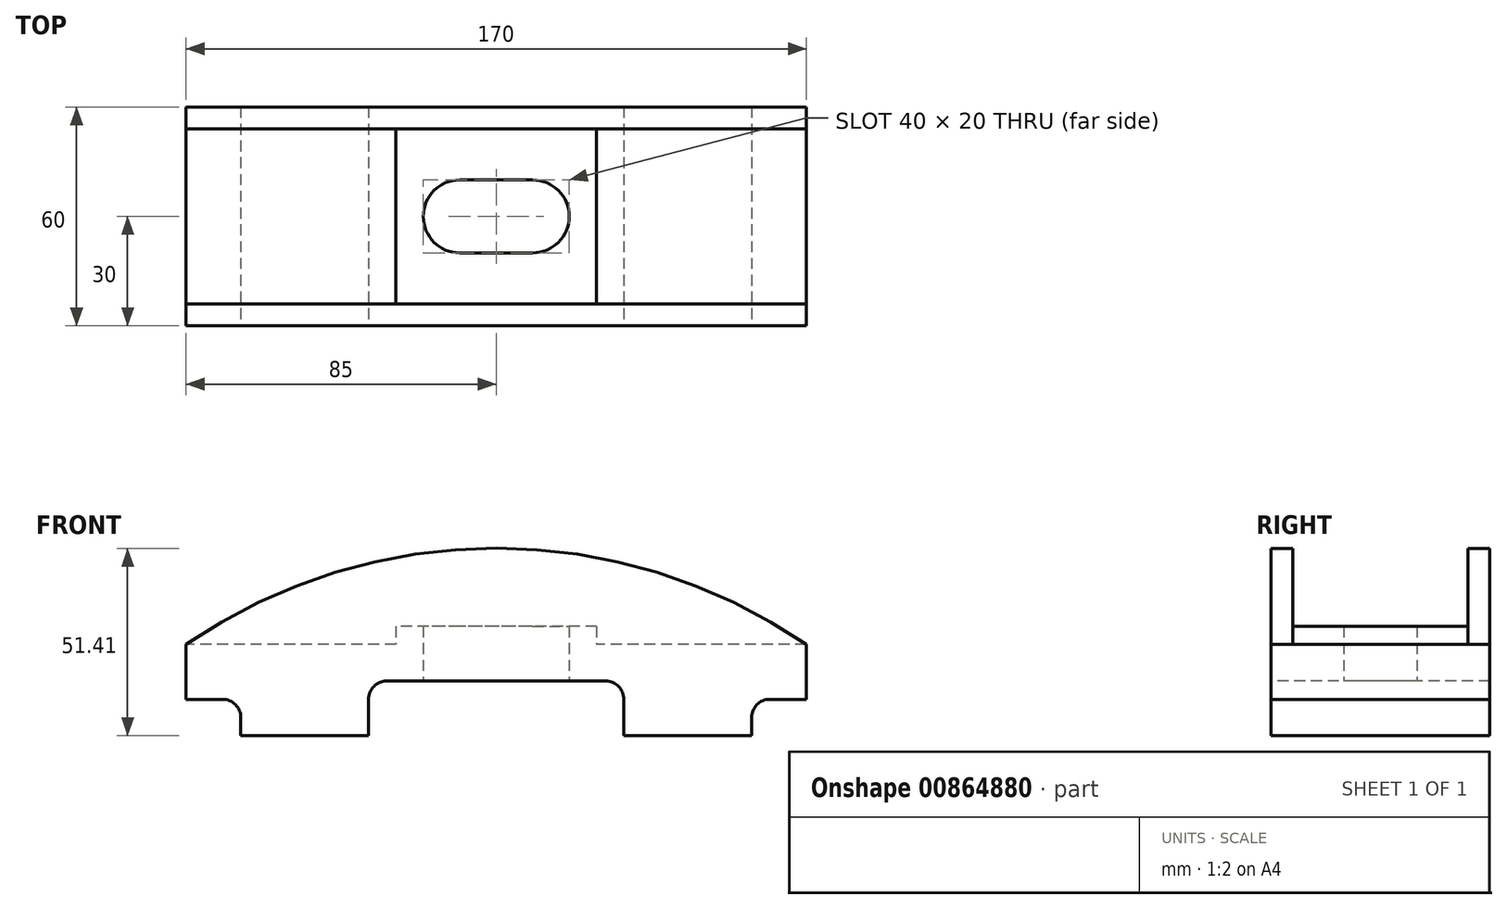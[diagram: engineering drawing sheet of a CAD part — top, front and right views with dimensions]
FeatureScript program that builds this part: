
annotation { "Feature Type Name" : "Feature", "Feature Type Description" : "" }
export const myFeature = defineFeature(function(context is Context, id is Id, definition is map)
    precondition{}
    {
        {
            var Q0;
            Q0=qCreatedBy(makeId("Top.planeOp"),FACE);
            var sketch = newSketch(context, id + "F0", { "sketchPlane" : qUnion([Q0])});
            skLineSegment(sketch, "E0.bottom", {"start": v(85, -30) * mm, "end": v(-85, -30) * mm});
            skLineSegment(sketch, "E0.top", {"start": v(85, 30) * mm, "end": v(-85, 30) * mm});
            skLineSegment(sketch, "E0.left", {"start": v(85, -30) * mm, "end": v(85, 30) * mm});
            skLineSegment(sketch, "E0.right", {"start": v(-85, -30) * mm, "end": v(-85, 30) * mm});
            skPoint(sketch, "E0.middle", {"position": v(0, 0) * mm});
            skSolve(sketch);
        }
        {
            var Q0;
            Q0 = qSketchRegion(id + "F0", true);
            extrude(context, id + "F1", {"entities" : qUnion([Q0]), "oppositeDirection" : true, "depth" : 25 * mm, "offsetDistance" : 25 * mm});
        }
        {
            var Q0;
            Q0=makeQuery(id+"F1.opExtrude","CAP_FACE",FACE,{"disambiguationData":[OSD([sQuery(id+"F0.wireOp",EDGE,"E0.bottom"),sQuery(id+"F0.wireOp",EDGE,"E0.top"),sQuery(id+"F0.wireOp",EDGE,"E0.left"),sQuery(id+"F0.wireOp",EDGE,"E0.right")])],"isStart":true});
            var sketch = newSketch(context, id + "F2", { "sketchPlane" : qUnion([Q0])});
            skLineSegment(sketch, "E1.bottom", {"start": v(27.5, -24) * mm, "end": v(-27.5, -24) * mm});
            skLineSegment(sketch, "E1.top", {"start": v(27.5, 24) * mm, "end": v(-27.5, 24) * mm});
            skLineSegment(sketch, "E1.left", {"start": v(27.5, -24) * mm, "end": v(27.5, 24) * mm});
            skLineSegment(sketch, "E1.right", {"start": v(-27.5, -24) * mm, "end": v(-27.5, 24) * mm});
            skPoint(sketch, "E1.middle", {"position": v(0, 0) * mm});
            skLineSegment(sketch, "E2.bottom", {"start": v(10, -10) * mm, "end": v(-10, -10) * mm});
            skLineSegment(sketch, "E2.top", {"start": v(10, 10) * mm, "end": v(-10, 10) * mm});
            skLineSegment(sketch, "E2.left", {"start": v(10, -10) * mm, "end": v(10, 10) * mm});
            skLineSegment(sketch, "E2.right", {"start": v(-10, -10) * mm, "end": v(-10, 10) * mm});
            skCircle(sketch, "E3", {"center": v(-10, 0) * mm, "radius": 10 * mm});
            skCircle(sketch, "E4", {"center": v(10, 0) * mm, "radius": 10 * mm});
            skSolve(sketch);
        }
        {
            var Q0;
            Q0=makeQuery(id+"F2.imprint","IMPRINT",FACE,{"disambiguationData":[TD([[makeQuery(id+"F2.imprint","IMPRINT",EDGE,{"derivedFrom":sQuery(id+"F2.wireOp",EDGE,"E1.bottom")}),-1.0]])]});
            extrude(context, id + "F3", {"entities" : qUnion([Q0]), "operationType" : NewBodyOperationType.ADD, "depth" : 5 * mm, "offsetDistance" : 25 * mm});
        }
        {
            var Q0;
            Q0=makeQuery(id+"F3.boolean.opBoolean","SPLIT",FACE,{"disambiguationData":[TD([makeQuery(id+"F3.opExtrude","SWEPT_FACE",FACE,{"disambiguationData":[OSD([sQuery(id+"F2.wireOp",EDGE,"E2.bottom")])]})])],"derivedFrom":makeQuery(id+"F1.opExtrude","CAP_FACE",FACE,{"disambiguationData":[OSD([sQuery(id+"F0.wireOp",EDGE,"E0.bottom"),sQuery(id+"F0.wireOp",EDGE,"E0.top"),sQuery(id+"F0.wireOp",EDGE,"E0.left"),sQuery(id+"F0.wireOp",EDGE,"E0.right")])],"isStart":true})});
            extrude(context, id + "F4", {"entities" : qUnion([Q0]), "operationType" : NewBodyOperationType.REMOVE, "endBound" : BoundingType.THROUGH_ALL, "oppositeDirection" : true, "depth" : 25 * mm, "offsetDistance" : 25 * mm});
        }
        {
            var Q0;
            Q0=makeQuery(id+"F1.opExtrude","SWEPT_FACE",FACE,{"disambiguationData":[OSD([sQuery(id+"F0.wireOp",EDGE,"E0.bottom")])]});
            var sketch = newSketch(context, id + "F5", { "sketchPlane" : qUnion([Q0])});
            skArc(sketch, "E5", {"start": v(85, 0) * mm, "mid": v(0, 26.4) * mm, "end": v(-85, 0) * mm});
            skSolve(sketch);
        }
        {
            var Q0;
            Q0=makeQuery(id+"F1.opExtrude","SWEPT_FACE",FACE,{"disambiguationData":[OSD([sQuery(id+"F0.wireOp",EDGE,"E0.top")])]});
            var sketch = newSketch(context, id + "F6", { "sketchPlane" : qUnion([Q0])});
            skArc(sketch, "E6", {"start": v(85, 0) * mm, "mid": v(0, 26.4) * mm, "end": v(-85, 0) * mm});
            skSolve(sketch);
        }
        {
            var Q0;
            Q0=makeQuery(id+"F6.imprint","IMPRINT",FACE,{"disambiguationData":[TD([[makeQuery(id+"F6.imprint","IMPRINT",EDGE,{"derivedFrom":sQuery(id+"F6.wireOp",EDGE,"E6")}),1.0]])]});
            extrude(context, id + "F7", {"entities" : qUnion([Q0]), "operationType" : NewBodyOperationType.ADD, "oppositeDirection" : true, "depth" : 6 * mm, "offsetDistance" : 25 * mm});
        }
        {
            var Q0;
            Q0=makeQuery(id+"F5.imprint","IMPRINT",FACE,{"disambiguationData":[TD([[makeQuery(id+"F5.imprint","IMPRINT",EDGE,{"derivedFrom":sQuery(id+"F5.wireOp",EDGE,"E5")}),1.0]])]});
            extrude(context, id + "F8", {"entities" : qUnion([Q0]), "operationType" : NewBodyOperationType.ADD, "oppositeDirection" : true, "depth" : 6 * mm, "offsetDistance" : 25 * mm});
        }
        {
            var Q0;
            {var subQ0=sQuery(id+"F0.wireOp",EDGE,"E0.bottom");Q0=makeQuery(id+"F8.boolean.opBoolean","MERGE",FACE,{"derivedFrom":[makeQuery(id+"F1.opExtrude","SWEPT_FACE",FACE,{"disambiguationData":[OSD([subQ0])]}),makeQuery(id+"F8.opExtrude","CAP_FACE",FACE,{"disambiguationData":[OSD([subQ0,sQuery(id+"F5.wireOp",EDGE,"E5")])],"isStart":true})]});}
            var sketch = newSketch(context, id + "F9", { "sketchPlane" : qUnion([Q0])});
            skLineSegment(sketch, "E7", {"start": v(0, -25) * mm, "end": v(-35, -25) * mm});
            skLineSegment(sketch, "E8", {"start": v(0, -25) * mm, "end": v(35, -25) * mm});
            skLineSegment(sketch, "E9", {"start": v(-35, -25) * mm, "end": v(-35, -15) * mm});
            skLineSegment(sketch, "E10", {"start": v(-30, -10) * mm, "end": v(30, -10) * mm});
            skLineSegment(sketch, "E11", {"start": v(35, -15) * mm, "end": v(35, -25) * mm});
            skPoint(sketch, "E12.visualSharp", {"position": v(-35, -10) * mm});
            skArc(sketch, "E12.filletArc", {"start": v(-30, -10) * mm, "mid": v(-33.54, -11.46) * mm, "end": v(-35, -15) * mm});
            skPoint(sketch, "E13.visualSharp", {"position": v(35, -10) * mm});
            skArc(sketch, "E13.filletArc", {"start": v(35, -15) * mm, "mid": v(33.54, -11.46) * mm, "end": v(30, -10) * mm});
            skSolve(sketch);
        }
        {
            var Q0;
            Q0 = qSketchRegion(id + "F9", true);
            extrude(context, id + "F10", {"entities" : qUnion([Q0]), "operationType" : NewBodyOperationType.REMOVE, "endBound" : BoundingType.THROUGH_ALL, "oppositeDirection" : true, "depth" : 25 * mm, "offsetDistance" : 25 * mm});
        }
        {
            var Q0;
            {var subQ0=sQuery(id+"F0.wireOp",EDGE,"E0.bottom");Q0=makeQuery(id+"F8.boolean.opBoolean","MERGE",FACE,{"derivedFrom":[makeQuery(id+"F1.opExtrude","SWEPT_FACE",FACE,{"disambiguationData":[OSD([subQ0])]}),makeQuery(id+"F8.opExtrude","CAP_FACE",FACE,{"disambiguationData":[OSD([subQ0,sQuery(id+"F5.wireOp",EDGE,"E5")])],"isStart":true})]});}
            var sketch = newSketch(context, id + "F11", { "sketchPlane" : qUnion([Q0])});
            skLineSegment(sketch, "E14", {"start": v(-85, -25) * mm, "end": v(-70, -25) * mm});
            skLineSegment(sketch, "E15", {"start": v(-70, -25) * mm, "end": v(-70, -20) * mm});
            skLineSegment(sketch, "E16", {"start": v(-75, -15) * mm, "end": v(-85, -15) * mm});
            skLineSegment(sketch, "E17", {"start": v(85, -25) * mm, "end": v(85, -15) * mm});
            skLineSegment(sketch, "E18", {"start": v(85, -15) * mm, "end": v(75, -15) * mm});
            skLineSegment(sketch, "E19", {"start": v(70, -20) * mm, "end": v(70, -25) * mm});
            skPoint(sketch, "E20.visualSharp", {"position": v(-70, -15) * mm});
            skArc(sketch, "E20.filletArc", {"start": v(-70, -20) * mm, "mid": v(-71.46, -16.46) * mm, "end": v(-75, -15) * mm});
            skPoint(sketch, "E21.visualSharp", {"position": v(70, -15) * mm});
            skArc(sketch, "E21.filletArc", {"start": v(75, -15) * mm, "mid": v(71.46, -16.46) * mm, "end": v(70, -20) * mm});
            skSolve(sketch);
        }
        {
            var Q0;
            {var subQ1=sQuery(id+"F11.wireOp",EDGE,"E14");Q0=makeQuery(id+"F11.imprint","IMPRINT",FACE,{"disambiguationData":[TD([[makeQuery(id+"F11.imprint","IMPRINT",EDGE,{"derivedFrom":subQ1}),-1.0]])]});}
            var Q1;
            {var subQ0=sQuery(id+"F11.wireOp",EDGE,"E17");Q1=makeQuery(id+"F11.imprint","IMPRINT",FACE,{"disambiguationData":[TD([[makeQuery(id+"F11.imprint","IMPRINT",EDGE,{"derivedFrom":subQ0}),1.0]])]});}
            extrude(context, id + "F12", {"entities" : qUnion([Q0, Q1]), "operationType" : NewBodyOperationType.REMOVE, "endBound" : BoundingType.THROUGH_ALL, "oppositeDirection" : true, "depth" : 25 * mm, "offsetDistance" : 25 * mm});
        }
    });
